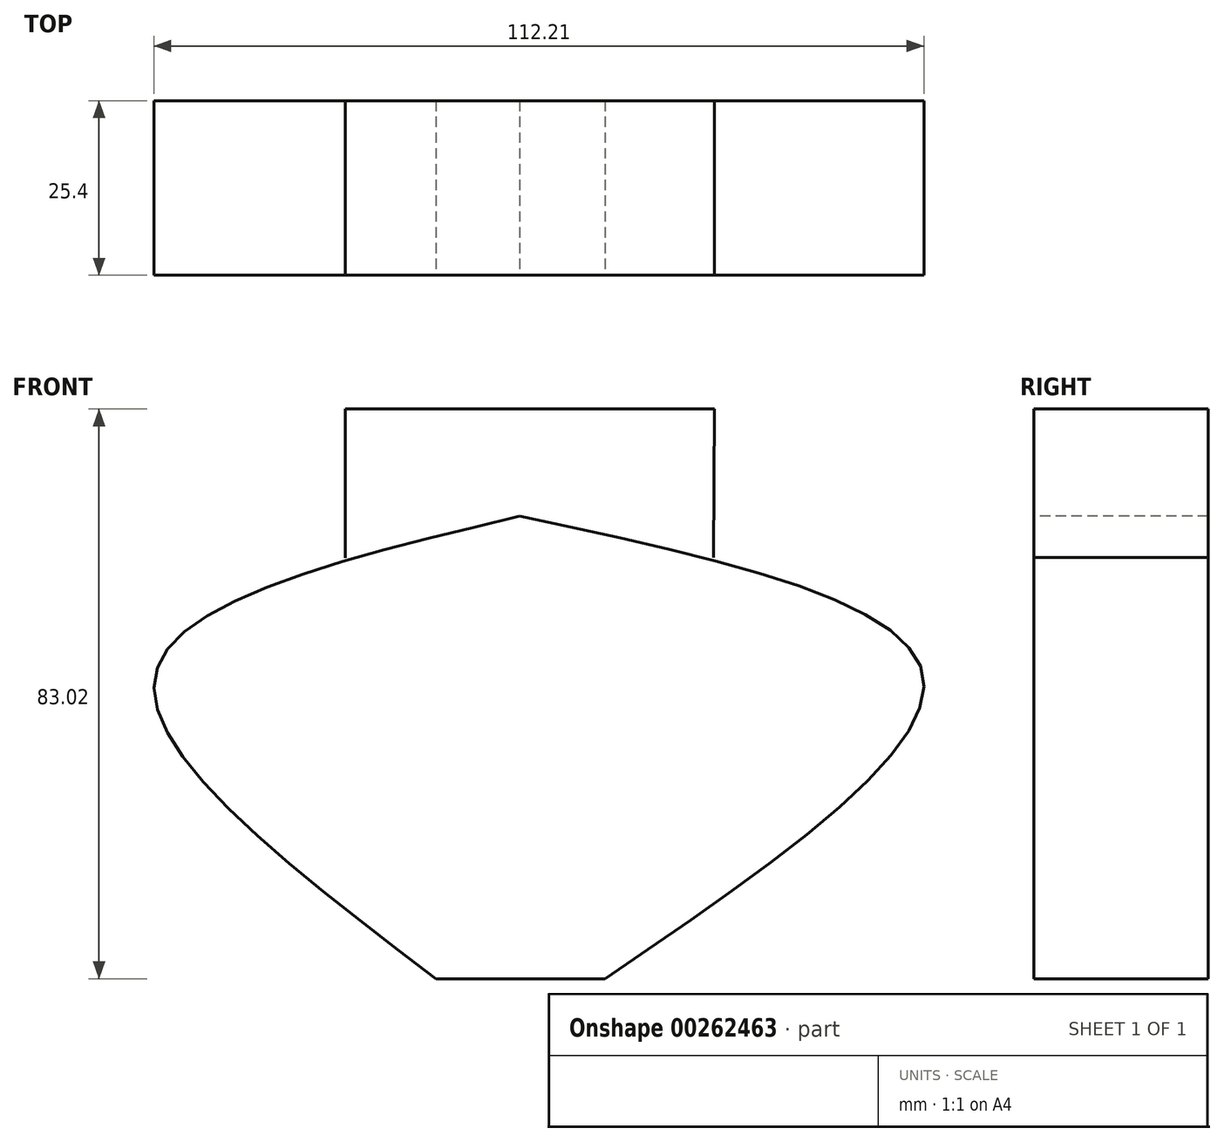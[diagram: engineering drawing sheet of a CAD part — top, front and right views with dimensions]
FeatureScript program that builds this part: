
annotation { "Feature Type Name" : "Feature", "Feature Type Description" : "" }
export const myFeature = defineFeature(function(context is Context, id is Id, definition is map)
    precondition{}
    {
        {
            var Q0;
            Q0=qCreatedBy(makeId("Front.planeOp"),FACE);
            var sketch = newSketch(context, id + "F0", { "sketchPlane" : qUnion([Q0])});
            skLineSegment(sketch, "E0", {"start": v(0, -44.22) * mm, "end": v(-12.18, -44.22) * mm});
            skFitSpline(sketch, "E1", {"points": [v(-12.18, -44.22) * mm, v(-53.09, 0) * mm, v(0, 23.16) * mm], "startDerivative": vector(-128.54, 97.87) * mm, "endDerivative": vector(153.83, 36.68) * mm});
            skLineSegment(sketch, "E2", {"start": v(0, -44.22) * mm, "end": v(12.48, -44.22) * mm});
            skFitSpline(sketch, "E3", {"points": [v(12.48, -44.22) * mm, v(58.8, 0) * mm, v(0, 23.16) * mm], "startDerivative": vector(145.1, 98.6) * mm, "endDerivative": vector(-170.4, 36.1) * mm});
            skLineSegment(sketch, "E4", {"start": v(-25.39, 17.1) * mm, "end": v(-25.39, 38.8) * mm});
            skLineSegment(sketch, "E5", {"start": v(-25.39, 38.8) * mm, "end": v(28.42, 38.8) * mm});
            skLineSegment(sketch, "E6", {"start": v(28.3, 17.17) * mm, "end": v(28.42, 38.8) * mm});
            skSolve(sketch);
        }
        {
            var Q0;
            Q0=sQuery(id+"F0.wireOp",EDGE,"E1");
            var Q1;
            Q1=sQuery(id+"F0.wireOp",EDGE,"E3");
            var Q2;
            Q2=sQuery(id+"F0.wireOp",EDGE,"E6");
            var Q3;
            Q3=sQuery(id+"F0.wireOp",EDGE,"E5");
            var Q4;
            Q4=sQuery(id+"F0.wireOp",EDGE,"E4");
            var Q5;
            Q5=sQuery(id+"F0.wireOp",EDGE,"E0");
            var Q6;
            Q6=sQuery(id+"F0.wireOp",EDGE,"E2");
            extrude(context, id + "F1", {"bodyType" : ToolBodyType.SURFACE, "surfaceEntities" : qUnion([Q0, Q1, Q2, Q3, Q4, Q5, Q6]), "depth" : 25.4 * mm});
        }
    });
